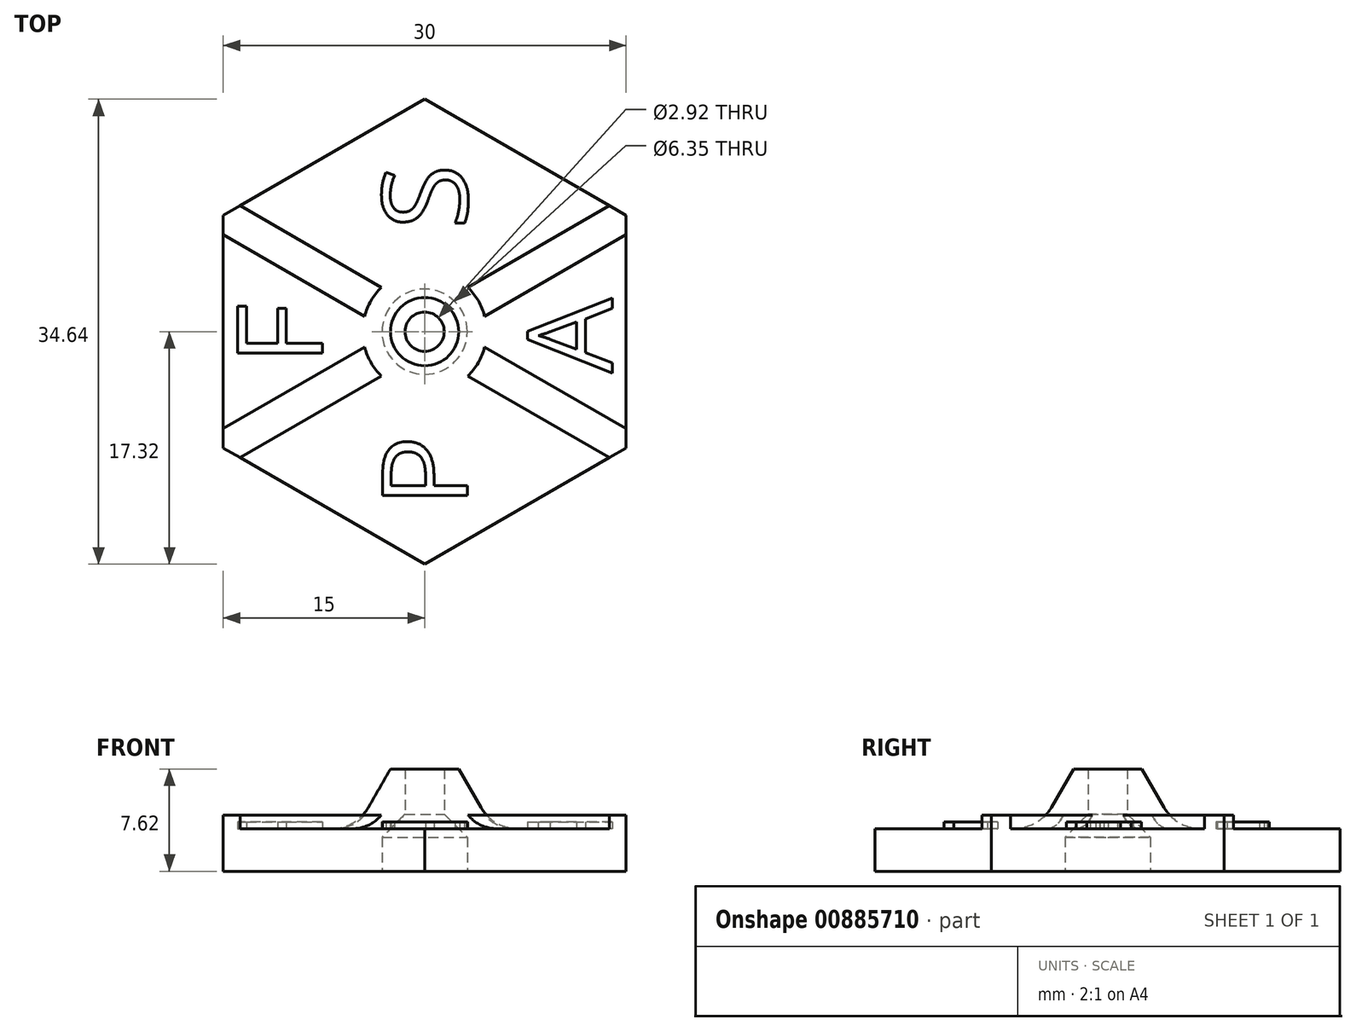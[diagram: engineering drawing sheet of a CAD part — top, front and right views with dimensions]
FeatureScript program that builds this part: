
annotation { "Feature Type Name" : "Feature", "Feature Type Description" : "" }
export const myFeature = defineFeature(function(context is Context, id is Id, definition is map)
    precondition{}
    {
        {
            var Q0;
            Q0=qCreatedBy(makeId("Top.planeOp"),FACE);
            var sketch = newSketch(context, id + "F0", { "sketchPlane" : qUnion([Q0])});
            skCircle(sketch, "E0.cCircle", {"center": v(0, 0) * mm, "radius": 15 * mm, "construction": true});
            skLineSegment(sketch, "E0.0", {"start": v(15, 8.66) * mm, "end": v(15, -8.66) * mm});
            skLineSegment(sketch, "E0.1", {"start": v(15, -8.66) * mm, "end": v(0, -17.32) * mm});
            skLineSegment(sketch, "E0.2", {"start": v(0, -17.32) * mm, "end": v(-15, -8.66) * mm});
            skLineSegment(sketch, "E0.3", {"start": v(-15, -8.66) * mm, "end": v(-15, 8.66) * mm});
            skLineSegment(sketch, "E0.4", {"start": v(-15, 8.66) * mm, "end": v(0, 17.32) * mm});
            skLineSegment(sketch, "E0.5", {"start": v(0, 17.32) * mm, "end": v(15, 8.66) * mm});
            skPoint(sketch, "E0.0.midPoint", {"position": v(15, 0) * mm});
            skCircle(sketch, "E1", {"center": v(0, 0) * mm, "radius": 4.76 * mm});
            skSolve(sketch);
        }
        {
            var Q0;
            Q0 = qSketchRegion(id + "F0", true);
            extrude(context, id + "F1", {"entities" : qUnion([Q0]), "depth" : 3.17 * mm, "offsetDistance" : 25.4 * mm});
        }
        {
            var Q0;
            Q0=qCreatedBy(makeId("Front.planeOp"),FACE);
            var sketch = newSketch(context, id + "F2", { "sketchPlane" : qUnion([Q0])});
            skLineSegment(sketch, "E2.0", {"start": v(-4.76, 3.18) * mm, "end": v(4.76, 3.18) * mm, "construction": true});
            skLineSegment(sketch, "E2.1", {"start": v(-4.76, 0) * mm, "end": v(4.76, 0) * mm, "construction": true});
            skLineSegment(sketch, "E3", {"start": v(4.76, 0) * mm, "end": v(4.76, 3.18) * mm});
            skLineSegment(sketch, "E4", {"start": v(4.76, 0) * mm, "end": v(3.18, 0) * mm});
            skLineSegment(sketch, "E5", {"start": v(3.18, 0) * mm, "end": v(3.18, 2.54) * mm});
            skLineSegment(sketch, "E6", {"start": v(3.18, 2.54) * mm, "end": v(1.46, 4.25) * mm});
            skLineSegment(sketch, "E7", {"start": v(1.46, 4.25) * mm, "end": v(1.46, 7.62) * mm});
            skLineSegment(sketch, "E8", {"start": v(1.46, 7.62) * mm, "end": v(2.54, 7.62) * mm});
            skLineSegment(sketch, "E9", {"start": v(2.54, 7.62) * mm, "end": v(4.19, 4.76) * mm});
            skLineSegment(sketch, "E10", {"start": v(4.76, 3.18) * mm, "end": v(6.94, 3.18) * mm});
            skArc(sketch, "E11", {"start": v(4.19, 4.76) * mm, "mid": v(5.35, 3.6) * mm, "end": v(6.94, 3.18) * mm});
            skLineSegment(sketch, "E12", {"start": v(0, 0) * mm, "end": v(0, 7.62) * mm, "construction": true});
            skSolve(sketch);
        }
        {
            var Q0;
            Q0 = qSketchRegion(id + "F2", true);
            var Q1;
            Q1=sQuery(id+"F2.wireOp",EDGE,"E12");
            revolve(context, id + "F3", {"operationType" : NewBodyOperationType.ADD, "surfaceOperationType" : NewSurfaceOperationType.NEW, "entities" : qUnion([Q0]), "axis" : qUnion([Q1]), "revolveType" : RevolveType.FULL});
        }
        {
            var Q0;
            Q0=makeQuery(id+"F1.opExtrude","CAP_FACE",FACE,{"disambiguationData":[OSD([sQuery(id+"F0.wireOp",EDGE,"E0.0"),sQuery(id+"F0.wireOp",EDGE,"E0.1"),sQuery(id+"F0.wireOp",EDGE,"E0.2"),sQuery(id+"F0.wireOp",EDGE,"E0.3"),sQuery(id+"F0.wireOp",EDGE,"E0.4"),sQuery(id+"F0.wireOp",EDGE,"E0.5"),sQuery(id+"F0.wireOp",EDGE,"E1")])],"isStart":false});
            var sketch = newSketch(context, id + "F4", { "sketchPlane" : qUnion([Q0])});
            skLineSegment(sketch, "E13.4", {"start": v(15, -8.66) * mm, "end": v(13.76, -9.38) * mm});
            skLineSegment(sketch, "E13.5", {"start": v(15, -7.22) * mm, "end": v(15, -8.66) * mm});
            skLineSegment(sketch, "E14", {"start": v(13.76, -9.38) * mm, "end": v(2.84, -3.08) * mm});
            skLineSegment(sketch, "E15", {"start": v(2.84, -3.08) * mm, "end": v(4.09, -0.92) * mm});
            skLineSegment(sketch, "E16", {"start": v(4.09, -0.92) * mm, "end": v(15, -7.22) * mm});
            skLineSegment(sketch, "E17.1.0", {"start": v(13.76, 9.38) * mm, "end": v(15, 8.66) * mm});
            skLineSegment(sketch, "E17.1.1", {"start": v(15, 8.66) * mm, "end": v(15, 7.22) * mm});
            skLineSegment(sketch, "E17.1.2", {"start": v(15, 7.22) * mm, "end": v(4.09, 0.92) * mm});
            skLineSegment(sketch, "E17.1.3", {"start": v(2.84, 3.08) * mm, "end": v(13.76, 9.38) * mm});
            skLineSegment(sketch, "E17.1.4", {"start": v(4.09, 0.92) * mm, "end": v(2.84, 3.08) * mm});
            skLineSegment(sketch, "E17.3.0", {"start": v(-15, 7.22) * mm, "end": v(-15, 8.66) * mm});
            skLineSegment(sketch, "E17.3.1", {"start": v(-15, 8.66) * mm, "end": v(-13.76, 9.38) * mm});
            skLineSegment(sketch, "E17.3.2", {"start": v(-13.76, 9.38) * mm, "end": v(-2.84, 3.08) * mm});
            skLineSegment(sketch, "E17.3.3", {"start": v(-4.09, 0.92) * mm, "end": v(-15, 7.22) * mm});
            skLineSegment(sketch, "E17.3.4", {"start": v(-2.84, 3.08) * mm, "end": v(-4.09, 0.92) * mm});
            skLineSegment(sketch, "E17.4.0", {"start": v(-13.76, -9.38) * mm, "end": v(-15, -8.66) * mm});
            skLineSegment(sketch, "E17.4.1", {"start": v(-15, -8.66) * mm, "end": v(-15, -7.22) * mm});
            skLineSegment(sketch, "E17.4.2", {"start": v(-15, -7.22) * mm, "end": v(-4.09, -0.92) * mm});
            skLineSegment(sketch, "E17.4.3", {"start": v(-2.84, -3.08) * mm, "end": v(-13.76, -9.38) * mm});
            skLineSegment(sketch, "E17.4.4", {"start": v(-4.09, -0.92) * mm, "end": v(-2.84, -3.08) * mm});
            skPoint(sketch, "E17.center", {"position": v(0, 0) * mm});
            skSolve(sketch);
        }
        {
            var Q0;
            Q0 = qSketchRegion(id + "F4", true);
            extrude(context, id + "F5", {"entities" : qUnion([Q0]), "operationType" : NewBodyOperationType.ADD, "depth" : 1.02 * mm, "offsetDistance" : 25.4 * mm});
        }
        {
            var Q0;
            {var subQ0=sQuery(id+"F0.wireOp",EDGE,"E0.3");Q0=makeQuery(id+"F5.boolean.opBoolean","SPLIT",FACE,{"disambiguationData":[TD([makeQuery(id+"F1.opExtrude","SWEPT_FACE",FACE,{"disambiguationData":[OSD([subQ0])]})])],"derivedFrom":makeQuery(id+"F1.opExtrude","CAP_FACE",FACE,{"disambiguationData":[OSD([sQuery(id+"F0.wireOp",EDGE,"E0.0"),sQuery(id+"F0.wireOp",EDGE,"E0.1"),sQuery(id+"F0.wireOp",EDGE,"E0.2"),subQ0,sQuery(id+"F0.wireOp",EDGE,"E0.4"),sQuery(id+"F0.wireOp",EDGE,"E0.5"),sQuery(id+"F0.wireOp",EDGE,"E1")])],"isStart":false})});}
            var sketch = newSketch(context, id + "F6", { "sketchPlane" : qUnion([Q0])});
            skText(sketch, "E18", { "text": "F", "fontName": "OpenSans-Regular.ttf"});
            skText(sketch, "E19", { "text": "S", "fontName": "OpenSans-Regular.ttf"});
            skText(sketch, "E20", { "text": "P", "fontName": "OpenSans-Regular.ttf"});
            skText(sketch, "E21", { "text": "A", "fontName": "OpenSans-Regular.ttf"});
            skLineSegment(sketch, "E22", {"start": v(0, -7.62) * mm, "end": v(0, 0) * mm, "construction": true});
            skLineSegment(sketch, "E23", {"start": v(0, 0) * mm, "end": v(0, 7.62) * mm, "construction": true});
            skLineSegment(sketch, "E24", {"start": v(-7.62, 0) * mm, "end": v(0, 0) * mm, "construction": true});
            skLineSegment(sketch, "E25", {"start": v(7.62, 0) * mm, "end": v(0, 0) * mm, "construction": true});
            const initialGuessF6  = {"E18": [-0.00762, -0.00247, 0, 1, 0.00635], "E19": [0.00317, 0.00762, 0, 1, 0.00635], "E20": [0.00317, -0.01305, 0, 1, 0.00635], "E21": [0.01397, -0.00308, 0, 1, 0.00635]};
            skSetInitialGuess(sketch, initialGuessF6);
            skSolve(sketch);
        }
        {
            var Q0;
            Q0 = qSketchRegion(id + "F6", true);
            extrude(context, id + "F7", {"entities" : qUnion([Q0]), "operationType" : NewBodyOperationType.ADD, "depth" : 0.5 * mm, "offsetDistance" : 25.4 * mm});
        }
    });
